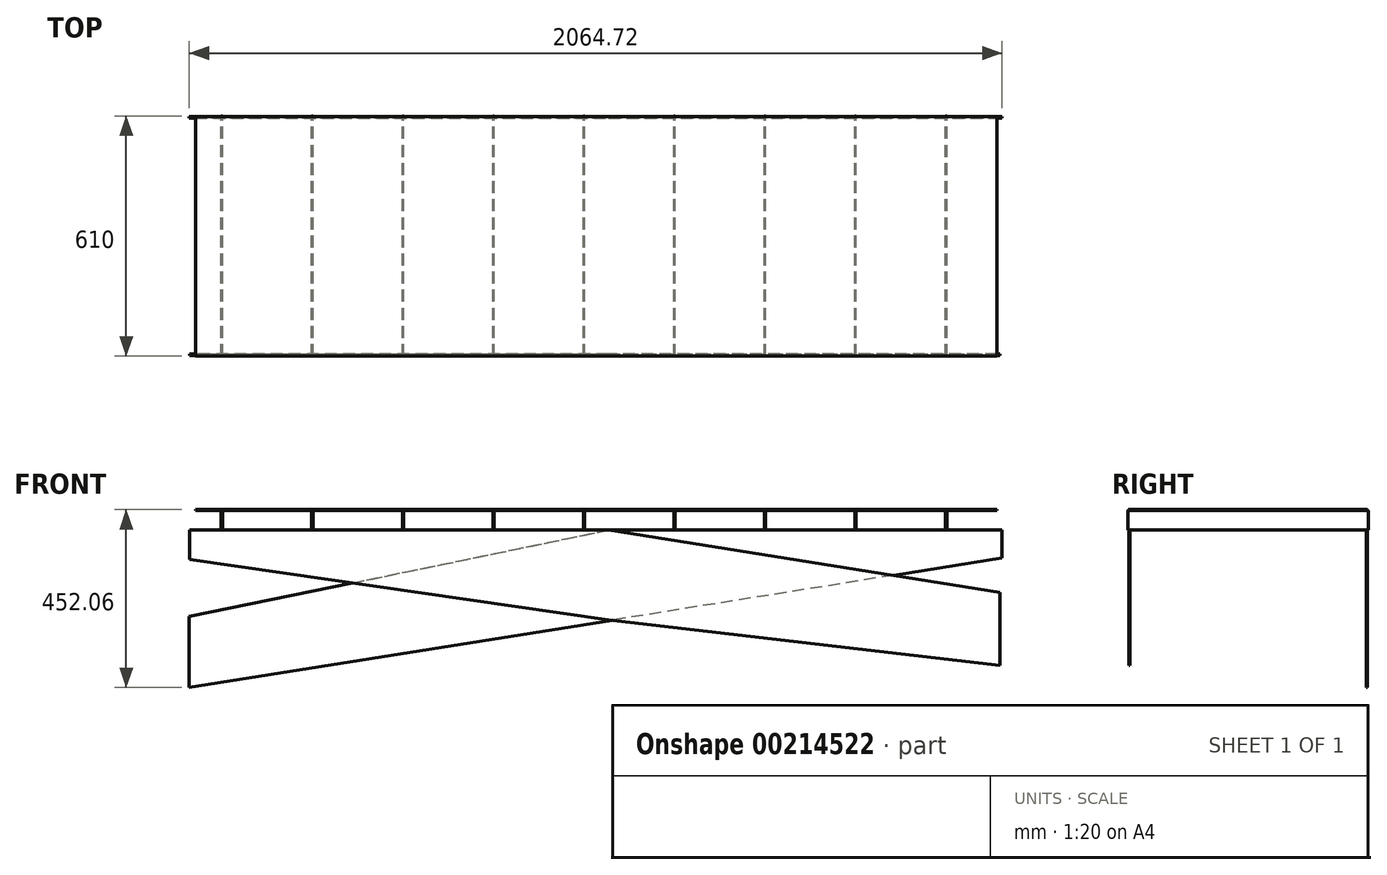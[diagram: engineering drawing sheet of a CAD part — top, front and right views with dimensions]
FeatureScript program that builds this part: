
annotation { "Feature Type Name" : "Feature", "Feature Type Description" : "" }
export const myFeature = defineFeature(function(context is Context, id is Id, definition is map)
    precondition{}
    {
        {
            var Q0;
            Q0=qCreatedBy(makeId("Front.planeOp"),FACE);
            var sketch = newSketch(context, id + "F0", { "sketchPlane" : qUnion([Q0])});
            skLineSegment(sketch, "E0", {"start": v(0, 0) * mm, "end": v(1000, 0) * mm});
            skLineSegment(sketch, "E1", {"start": v(1000, 0) * mm, "end": v(1000, -71.2) * mm});
            skLineSegment(sketch, "E2", {"start": v(1000, -71.2) * mm, "end": v(-1064.72, -400.06) * mm});
            skLineSegment(sketch, "E3", {"start": v(-1064.72, -400.06) * mm, "end": v(-1064.72, -220.06) * mm});
            skLineSegment(sketch, "E4", {"start": v(-1064.72, -220.06) * mm, "end": v(0, 0) * mm});
            skSolve(sketch);
        }
        {
            var Q0;
            Q0 = qSketchRegion(id + "F0", true);
            extrude(context, id + "F1", {"entities" : qUnion([Q0]), "depth" : 3 * mm, "offsetDistance" : 25 * mm});
        }
        {
            var Q0;
            Q0=makeQuery(id+"F1.opExtrude","CAP_FACE",FACE,{"disambiguationData":[OSD([sQuery(id+"F0.wireOp",EDGE,"E0"),sQuery(id+"F0.wireOp",EDGE,"E1"),sQuery(id+"F0.wireOp",EDGE,"E2"),sQuery(id+"F0.wireOp",EDGE,"E3"),sQuery(id+"F0.wireOp",EDGE,"E4")])],"isStart":false});
            cPlane(context, id + "F2", {"entities" : qUnion([Q0]), "cplaneType" : CPlaneType.OFFSET, "offset" : 600 * mm, "width" : 150 * mm, "height" : 150 * mm});
        }
        {
            var Q0;
            Q0=qCreatedBy(id+"F2.planeOp",FACE);
            var sketch = newSketch(context, id + "F3", { "sketchPlane" : qUnion([Q0])});
            skLineSegment(sketch, "E5", {"start": v(0, 0) * mm, "end": v(-1063.74, 0) * mm});
            skLineSegment(sketch, "E6", {"start": v(-1063.74, 0) * mm, "end": v(-1063.74, -74.73) * mm});
            skLineSegment(sketch, "E7", {"start": v(-1063.74, -74.73) * mm, "end": v(0, -227.94) * mm});
            skLineSegment(sketch, "E8", {"start": v(0, -227.94) * mm, "end": v(994.62, -344.51) * mm});
            skLineSegment(sketch, "E9", {"start": v(994.62, -344.51) * mm, "end": v(994.62, -158) * mm});
            skLineSegment(sketch, "E10", {"start": v(994.62, -158) * mm, "end": v(0, 0) * mm});
            skSolve(sketch);
        }
        {
            var Q0;
            Q0 = qSketchRegion(id + "F3", true);
            extrude(context, id + "F4", {"entities" : qUnion([Q0]), "depth" : 3 * mm, "offsetDistance" : 25 * mm});
        }
        {
            var Q0;
            Q0=qCreatedBy(id+"F2.planeOp",FACE);
            cPlane(context, id + "F5", {"entities" : qUnion([Q0]), "cplaneType" : CPlaneType.OFFSET, "offset" : 300 * mm, "oppositeDirection" : true, "width" : 150 * mm, "height" : 150 * mm});
        }
        {
            var Q0;
            Q0=qCreatedBy(id+"F5.planeOp",FACE);
            var sketch = newSketch(context, id + "F6", { "sketchPlane" : qUnion([Q0])});
            skLineSegment(sketch, "E11.bottom", {"start": v(-983.5, 0) * mm, "end": v(-980.5, 0) * mm});
            skLineSegment(sketch, "E11.top", {"start": v(-983.5, 50) * mm, "end": v(-980.5, 50) * mm});
            skLineSegment(sketch, "E11.left", {"start": v(-983.5, 0) * mm, "end": v(-983.5, 50) * mm});
            skLineSegment(sketch, "E11.right", {"start": v(-980.5, 0) * mm, "end": v(-980.5, 50) * mm});
            skLineSegment(sketch, "E12.1.0.0", {"start": v(-753.5, 0) * mm, "end": v(-750.5, 0) * mm});
            skLineSegment(sketch, "E12.1.0.1", {"start": v(-750.5, 0) * mm, "end": v(-750.5, 50) * mm});
            skLineSegment(sketch, "E12.1.0.2", {"start": v(-753.5, 50) * mm, "end": v(-750.5, 50) * mm});
            skLineSegment(sketch, "E12.1.0.3", {"start": v(-753.5, 0) * mm, "end": v(-753.5, 50) * mm});
            skLineSegment(sketch, "E12.2.0.0", {"start": v(-523.5, 0) * mm, "end": v(-520.5, 0) * mm});
            skLineSegment(sketch, "E12.2.0.1", {"start": v(-520.5, 0) * mm, "end": v(-520.5, 50) * mm});
            skLineSegment(sketch, "E12.2.0.2", {"start": v(-523.5, 50) * mm, "end": v(-520.5, 50) * mm});
            skLineSegment(sketch, "E12.2.0.3", {"start": v(-523.5, 0) * mm, "end": v(-523.5, 50) * mm});
            skLineSegment(sketch, "E12.3.0.0", {"start": v(-293.5, 0) * mm, "end": v(-290.5, 0) * mm});
            skLineSegment(sketch, "E12.3.0.1", {"start": v(-290.5, 0) * mm, "end": v(-290.5, 50) * mm});
            skLineSegment(sketch, "E12.3.0.2", {"start": v(-293.5, 50) * mm, "end": v(-290.5, 50) * mm});
            skLineSegment(sketch, "E12.3.0.3", {"start": v(-293.5, 0) * mm, "end": v(-293.5, 50) * mm});
            skLineSegment(sketch, "E12.4.0.0", {"start": v(-63.5, 0) * mm, "end": v(-60.5, 0) * mm});
            skLineSegment(sketch, "E12.4.0.1", {"start": v(-60.5, 0) * mm, "end": v(-60.5, 50) * mm});
            skLineSegment(sketch, "E12.4.0.2", {"start": v(-63.5, 50) * mm, "end": v(-60.5, 50) * mm});
            skLineSegment(sketch, "E12.4.0.3", {"start": v(-63.5, 0) * mm, "end": v(-63.5, 50) * mm});
            skLineSegment(sketch, "E12.5.0.0", {"start": v(166.5, 0) * mm, "end": v(169.5, 0) * mm});
            skLineSegment(sketch, "E12.5.0.1", {"start": v(169.5, 0) * mm, "end": v(169.5, 50) * mm});
            skLineSegment(sketch, "E12.5.0.2", {"start": v(166.5, 50) * mm, "end": v(169.5, 50) * mm});
            skLineSegment(sketch, "E12.5.0.3", {"start": v(166.5, 0) * mm, "end": v(166.5, 50) * mm});
            skLineSegment(sketch, "E12.6.0.0", {"start": v(396.5, 0) * mm, "end": v(399.5, 0) * mm});
            skLineSegment(sketch, "E12.6.0.1", {"start": v(399.5, 0) * mm, "end": v(399.5, 50) * mm});
            skLineSegment(sketch, "E12.6.0.2", {"start": v(396.5, 50) * mm, "end": v(399.5, 50) * mm});
            skLineSegment(sketch, "E12.6.0.3", {"start": v(396.5, 0) * mm, "end": v(396.5, 50) * mm});
            skLineSegment(sketch, "E12.7.0.0", {"start": v(626.5, 0) * mm, "end": v(629.5, 0) * mm});
            skLineSegment(sketch, "E12.7.0.1", {"start": v(629.5, 0) * mm, "end": v(629.5, 50) * mm});
            skLineSegment(sketch, "E12.7.0.2", {"start": v(626.5, 50) * mm, "end": v(629.5, 50) * mm});
            skLineSegment(sketch, "E12.7.0.3", {"start": v(626.5, 0) * mm, "end": v(626.5, 50) * mm});
            skLineSegment(sketch, "E12.8.0.0", {"start": v(856.5, 0) * mm, "end": v(859.5, 0) * mm});
            skLineSegment(sketch, "E12.8.0.1", {"start": v(859.5, 0) * mm, "end": v(859.5, 50) * mm});
            skLineSegment(sketch, "E12.8.0.2", {"start": v(856.5, 50) * mm, "end": v(859.5, 50) * mm});
            skLineSegment(sketch, "E12.8.0.3", {"start": v(856.5, 0) * mm, "end": v(856.5, 50) * mm});
            skLineSegment(sketch, "E12.direction1", {"start": v(-983.5, 0) * mm, "end": v(-753.5, 0) * mm, "construction": true});
            skSolve(sketch);
        }
        {
            var Q0;
            Q0 = qSketchRegion(id + "F6", true);
            extrude(context, id + "F7", {"entities" : qUnion([Q0]), "endBound" : BoundingType.SYMMETRIC, "depth" : 610 * mm, "offsetDistance" : 25 * mm});
        }
        {
            var Q0;
            Q0=makeQuery(id+"F7.opExtrude","SWEPT_FACE",FACE,{"disambiguationData":[OSD([sQuery(id+"F6.wireOp",EDGE,"E11.top")])]});
            var sketch = newSketch(context, id + "F8", { "sketchPlane" : qUnion([Q0])});
            skLineSegment(sketch, "E13.bottom", {"start": v(-1049.2, 0) * mm, "end": v(987.45, 0) * mm});
            skLineSegment(sketch, "E13.top", {"start": v(-1049.2, -607.42) * mm, "end": v(987.45, -607.42) * mm});
            skLineSegment(sketch, "E13.left", {"start": v(-1049.2, 0) * mm, "end": v(-1049.2, -607.42) * mm});
            skLineSegment(sketch, "E13.right", {"start": v(987.45, 0) * mm, "end": v(987.45, -607.42) * mm});
            skSolve(sketch);
        }
        {
            var Q0;
            Q0 = qSketchRegion(id + "F8", true);
            extrude(context, id + "F9", {"entities" : qUnion([Q0]), "depth" : 2 * mm, "offsetDistance" : 25 * mm});
        }
    });
